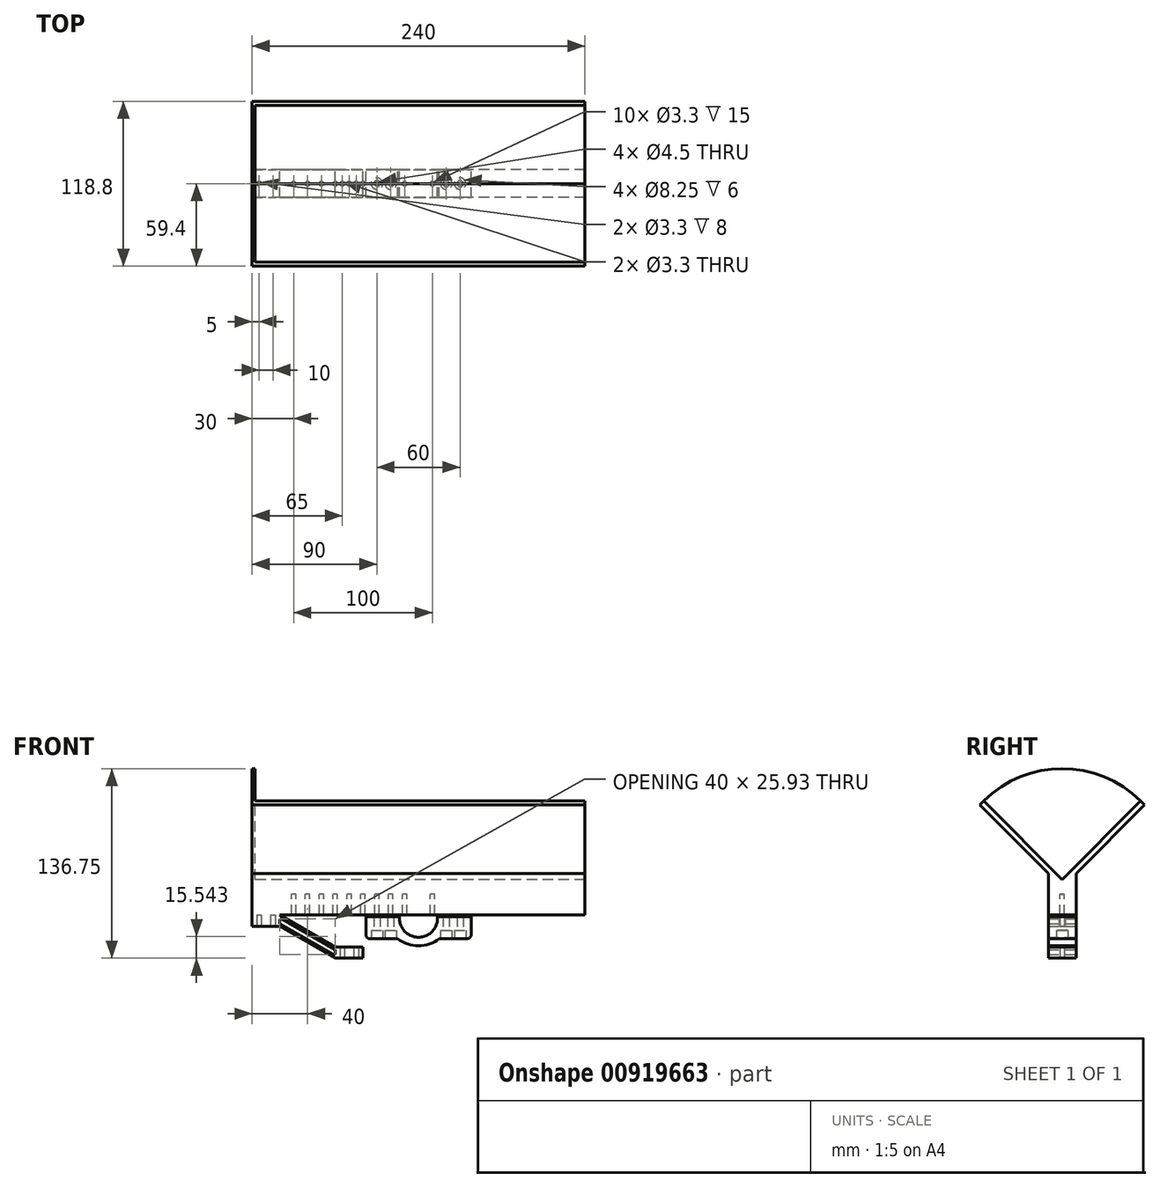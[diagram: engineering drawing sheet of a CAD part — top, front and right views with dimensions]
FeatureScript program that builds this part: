
annotation { "Feature Type Name" : "Feature", "Feature Type Description" : "" }
export const myFeature = defineFeature(function(context is Context, id is Id, definition is map)
    precondition{}
    {
        {
            var Q0;
            Q0=qCreatedBy(makeId("Right.planeOp"),FACE);
            var sketch = newSketch(context, id + "F0", { "sketchPlane" : qUnion([Q0])});
            skLineSegment(sketch, "E0.top", {"start": v(10, -15) * mm, "end": v(-10, -15) * mm});
            skLineSegment(sketch, "E0.left", {"start": v(10, 15) * mm, "end": v(10, -15) * mm});
            skLineSegment(sketch, "E0.right", {"start": v(-10, 15) * mm, "end": v(-10, -15) * mm});
            skPoint(sketch, "E0.middle", {"position": v(0, 0) * mm});
            skLineSegment(sketch, "E1", {"start": v(-10, 15) * mm, "end": v(-59.4, 64.4) * mm});
            skLineSegment(sketch, "E2", {"start": v(-59.4, 64.4) * mm, "end": v(-56.57, 67.23) * mm});
            skLineSegment(sketch, "E3", {"start": v(-56.57, 67.23) * mm, "end": v(0, 10.66) * mm});
            skLineSegment(sketch, "E4.MirrorCS", {"start": v(56.57, 67.23) * mm, "end": v(0, 10.66) * mm});
            skLineSegment(sketch, "E5.MirrorCS", {"start": v(10, 15) * mm, "end": v(59.4, 64.4) * mm});
            skLineSegment(sketch, "E6.MirrorCS", {"start": v(59.4, 64.4) * mm, "end": v(56.57, 67.23) * mm});
            skSolve(sketch);
        }
        {
            var Q0;
            Q0=qSketchRegion(id+"F0",true);
            extrude(context, id + "F1", {"entities" : qUnion([Q0]), "depth" : 120 * mm, "offsetDistance" : 25 * mm, "hasSecondDirection" : true, "secondDirectionOppositeDirection" : true, "secondDirectionDepth" : 120 * mm});
        }
        {
            var Q0;
            Q0=qCreatedBy(makeId("Front.planeOp"),FACE);
            var sketch = newSketch(context, id + "F2", { "sketchPlane" : qUnion([Q0])});
            skLineSegment(sketch, "E7.bottom", {"start": v(-120, -15) * mm, "end": v(-100, -15) * mm});
            skLineSegment(sketch, "E7.top", {"start": v(-120, -23) * mm, "end": v(-102.68, -23) * mm});
            skLineSegment(sketch, "E7.left", {"start": v(-120, -15) * mm, "end": v(-120, -23) * mm});
            skLineSegment(sketch, "E8.bottom", {"start": v(-60, -46.1) * mm, "end": v(-40, -46.1) * mm});
            skLineSegment(sketch, "E8.top", {"start": v(-57.32, -38.1) * mm, "end": v(-40, -38.1) * mm});
            skLineSegment(sketch, "E8.right", {"start": v(-40, -46.1) * mm, "end": v(-40, -38.1) * mm});
            skLineSegment(sketch, "E9", {"start": v(-97.68, -24.34) * mm, "end": v(-60, -46.1) * mm});
            skLineSegment(sketch, "E10", {"start": v(-100, -15) * mm, "end": v(-62.32, -36.75) * mm});
            skLineSegment(sketch, "E11", {"start": v(-100, -21.15) * mm, "end": v(-61.5, -43.38) * mm});
            skLineSegment(sketch, "E12", {"start": v(-60, -42.51) * mm, "end": v(-60, -39.94) * mm});
            skLineSegment(sketch, "E13", {"start": v(-60, -39.94) * mm, "end": v(-98.5, -17.71) * mm});
            skLineSegment(sketch, "E14", {"start": v(-100, -18.58) * mm, "end": v(-100, -21.15) * mm});
            skPoint(sketch, "E15", {"position": v(-115, -23) * mm});
            skPoint(sketch, "E16", {"position": v(-105, -23) * mm});
            skPoint(sketch, "E17", {"position": v(-55, -46.1) * mm});
            skPoint(sketch, "E18", {"position": v(-45, -46.1) * mm});
            skPoint(sketch, "E19.visualSharp", {"position": v(-100, -23) * mm});
            skArc(sketch, "E19.filletArc", {"start": v(-97.68, -24.34) * mm, "mid": v(-100.1, -23.34) * mm, "end": v(-102.68, -23) * mm});
            skPoint(sketch, "E20.visualSharp", {"position": v(-60, -38.1) * mm});
            skArc(sketch, "E20.filletArc", {"start": v(-62.32, -36.75) * mm, "mid": v(-59.9, -37.75) * mm, "end": v(-57.32, -38.1) * mm});
            skPoint(sketch, "E21.visualSharp", {"position": v(-100, -16.85) * mm});
            skArc(sketch, "E21.filletArc", {"start": v(-98.5, -17.71) * mm, "mid": v(-99.5, -17.71) * mm, "end": v(-100, -18.58) * mm});
            skPoint(sketch, "E22.visualSharp", {"position": v(-60, -44.25) * mm});
            skArc(sketch, "E22.filletArc", {"start": v(-61.5, -43.38) * mm, "mid": v(-60.5, -43.38) * mm, "end": v(-60, -42.51) * mm});
            skSolve(sketch);
        }
        {
            var Q0;
            Q0=qSketchRegion(id+"F2",true);
            extrude(context, id + "F3", {"entities" : qUnion([Q0]), "depth" : 10 * mm, "offsetDistance" : 25 * mm, "hasSecondDirection" : true, "secondDirectionOppositeDirection" : true, "secondDirectionDepth" : 10 * mm});
        }
        {
            var Q0;
            Q0=qCreatedBy(makeId("Top.planeOp"),FACE);
            var sketch = newSketch(context, id + "F4", { "sketchPlane" : qUnion([Q0])});
            skCircle(sketch, "E23", {"center": v(-90, 0) * mm, "radius": 2.5 * mm});
            skCircle(sketch, "E24.1.0.0", {"center": v(-80, 0) * mm, "radius": 2.5 * mm});
            skCircle(sketch, "E24.2.0.0", {"center": v(-70, 0) * mm, "radius": 2.5 * mm});
            skCircle(sketch, "E24.3.0.0", {"center": v(-60, 0) * mm, "radius": 2.5 * mm});
            skCircle(sketch, "E24.4.0.0", {"center": v(-50, 0) * mm, "radius": 2.5 * mm});
            skCircle(sketch, "E24.5.0.0", {"center": v(-40, 0) * mm, "radius": 2.5 * mm});
            skCircle(sketch, "E24.6.0.0", {"center": v(-30, 0) * mm, "radius": 2.5 * mm});
            skCircle(sketch, "E24.7.0.0", {"center": v(-20, 0) * mm, "radius": 2.5 * mm});
            skCircle(sketch, "E24.8.0.0", {"center": v(-10, 0) * mm, "radius": 2.5 * mm});
            skCircle(sketch, "E24.9.0.0", {"center": v(0, 0) * mm, "radius": 2.5 * mm});
            skCircle(sketch, "E24.10.0.0", {"center": v(10, 0) * mm, "radius": 2.5 * mm});
            skCircle(sketch, "E24.11.0.0", {"center": v(20, 0) * mm, "radius": 2.5 * mm});
            skCircle(sketch, "E24.12.0.0", {"center": v(30, 0) * mm, "radius": 2.5 * mm});
            skCircle(sketch, "E24.13.0.0", {"center": v(40, 0) * mm, "radius": 2.5 * mm});
            skCircle(sketch, "E24.14.0.0", {"center": v(50, 0) * mm, "radius": 2.5 * mm});
            skCircle(sketch, "E24.15.0.0", {"center": v(60, 0) * mm, "radius": 2.5 * mm});
            skCircle(sketch, "E24.16.0.0", {"center": v(70, 0) * mm, "radius": 2.5 * mm});
            skLineSegment(sketch, "E24.direction1", {"start": v(-90, 0) * mm, "end": v(-80, 0) * mm, "construction": true});
            skCircle(sketch, "E25.0.17.0", {"center": v(80, 0) * mm, "radius": 2.5 * mm});
            skCircle(sketch, "E25.0.18.0", {"center": v(90, 0) * mm, "radius": 2.5 * mm});
            skSolve(sketch);
        }
        {
            var Q0;
            Q0=sQuery(id+"F4.wireOp",VERTEX,"E23.center");
            var Q1;
            Q1=sQuery(id+"F4.wireOp",VERTEX,"E24.1.0.0.center");
            var Q2;
            Q2=sQuery(id+"F4.wireOp",VERTEX,"E24.2.0.0.center");
            var Q3;
            Q3=sQuery(id+"F4.wireOp",VERTEX,"E24.3.0.0.center");
            var Q4;
            Q4=sQuery(id+"F4.wireOp",VERTEX,"E24.4.0.0.center");
            var Q5;
            Q5=sQuery(id+"F4.wireOp",VERTEX,"E24.5.0.0.center");
            var Q6;
            Q6=sQuery(id+"F4.wireOp",VERTEX,"E24.6.0.0.center");
            var Q7;
            Q7=sQuery(id+"F4.wireOp",VERTEX,"E24.7.0.0.center");
            var Q8;
            Q8=sQuery(id+"F4.wireOp",VERTEX,"E24.8.0.0.center");
            var Q9;
            Q9=sQuery(id+"F4.wireOp",VERTEX,"E24.10.0.0.center");
            var Q10;
            Q10=makeQuery(id+"F1.opExtrude","SWEPT_BODY",BODY,{"disambiguationData":[OSD([sQuery(id+"F0.wireOp",EDGE,"E0.top"),sQuery(id+"F0.wireOp",EDGE,"E0.left"),sQuery(id+"F0.wireOp",EDGE,"E0.right"),sQuery(id+"F0.wireOp",EDGE,"E1"),sQuery(id+"F0.wireOp",EDGE,"E2"),sQuery(id+"F0.wireOp",EDGE,"E3"),sQuery(id+"F0.wireOp",EDGE,"E4.MirrorCS"),sQuery(id+"F0.wireOp",EDGE,"E5.MirrorCS"),sQuery(id+"F0.wireOp",EDGE,"E6.MirrorCS")])]});
            hole(context, id + "F5", {"style" : HoleStyle.SIMPLE, "endStyle" : HoleEndStyle.THROUGH, "standardTappedOrClearance" : lookupTablePath({ "standard" : "ISO", "fit" : "Normal", "size" : "M3", "type" : "Clearance" }), "standardBlindInLast" : lookupTablePath({ "fit" : "Standard", "standard" : "ISO", "size" : "M3", "type" : "Clearance" }), "holeDiameter" : 3.3 * mm, "majorDiameter" : 5 * mm, "isTappedThrough" : true, "tappedDepth" : 12 * mm, "tapClearance" : 3, "locations" : qUnion([Q0, Q1, Q2, Q3, Q4, Q5, Q6, Q7, Q8, Q9]), "scope" : qUnion([Q10])});
        }
        {
            var Q0;
            Q0=makeQuery(id+"F3.opExtrude","SWEPT_FACE",FACE,{"disambiguationData":[OSD([sQuery(id+"F2.wireOp",EDGE,"E7.top")])]});
            var sketch = newSketch(context, id + "F6", { "sketchPlane" : qUnion([Q0])});
            skCircle(sketch, "E26", {"center": v(-110, 0) * mm, "radius": 10 * mm});
            skLineSegment(sketch, "E27", {"start": v(-120, 0) * mm, "end": v(-110, 0) * mm, "construction": true});
            skLineSegment(sketch, "E28", {"start": v(-100, 0) * mm, "end": v(-110, 0) * mm, "construction": true});
            skPoint(sketch, "E29", {"position": v(-115, 0) * mm});
            skPoint(sketch, "E30", {"position": v(-105, 0) * mm});
            skSolve(sketch);
        }
        {
            var Q0;
            Q0=makeQuery(id+"F3.opExtrude","SWEPT_FACE",FACE,{"disambiguationData":[OSD([sQuery(id+"F2.wireOp",EDGE,"E8.bottom")])]});
            var sketch = newSketch(context, id + "F7", { "sketchPlane" : qUnion([Q0])});
            skCircle(sketch, "E31", {"center": v(-50, 0) * mm, "radius": 10 * mm});
            skLineSegment(sketch, "E32", {"start": v(-60, 0) * mm, "end": v(-50, 0) * mm, "construction": true});
            skLineSegment(sketch, "E33", {"start": v(-40, 0) * mm, "end": v(-50, 0) * mm, "construction": true});
            skPoint(sketch, "E34", {"position": v(-55, 0) * mm});
            skPoint(sketch, "E35", {"position": v(-45, 0) * mm});
            skSolve(sketch);
        }
        {
            var Q0;
            Q0=sQuery(id+"F7.wireOp",VERTEX,"E35");
            var Q1;
            Q1=sQuery(id+"F7.wireOp",VERTEX,"E34");
            var Q2;
            Q2=sQuery(id+"F6.wireOp",VERTEX,"E30");
            var Q3;
            Q3=sQuery(id+"F6.wireOp",VERTEX,"E29");
            var Q4;
            Q4=makeQuery(id+"F3.opExtrude","SWEPT_BODY",BODY,{"disambiguationData":[OSD([sQuery(id+"F2.wireOp",EDGE,"E7.bottom"),sQuery(id+"F2.wireOp",EDGE,"E7.top"),sQuery(id+"F2.wireOp",EDGE,"E7.left"),sQuery(id+"F2.wireOp",EDGE,"E8.bottom"),sQuery(id+"F2.wireOp",EDGE,"E8.top"),sQuery(id+"F2.wireOp",EDGE,"E8.right"),sQuery(id+"F2.wireOp",EDGE,"E9"),sQuery(id+"F2.wireOp",EDGE,"E10"),sQuery(id+"F2.wireOp",EDGE,"E11"),sQuery(id+"F2.wireOp",EDGE,"E12"),sQuery(id+"F2.wireOp",EDGE,"E13"),sQuery(id+"F2.wireOp",EDGE,"E14")])]});
            hole(context, id + "F8", {"style" : HoleStyle.SIMPLE, "endStyle" : HoleEndStyle.THROUGH, "standardTappedOrClearance" : lookupTablePath({ "standard" : "ISO", "fit" : "Normal", "size" : "M3", "type" : "Clearance" }), "standardBlindInLast" : lookupTablePath({ "fit" : "Standard", "standard" : "ISO", "size" : "M3", "type" : "Clearance" }), "holeDiameter" : 3.3 * mm, "majorDiameter" : 5 * mm, "isTappedThrough" : true, "tappedDepth" : 12 * mm, "tapClearance" : 3, "locations" : qUnion([Q0, Q1, Q2, Q3]), "scope" : qUnion([Q4])});
        }
        {
            var Q0;
            Q0=makeQuery(id+"F1.opExtrude","CAP_FACE",FACE,{"disambiguationData":[OSD([sQuery(id+"F0.wireOp",EDGE,"E0.top"),sQuery(id+"F0.wireOp",EDGE,"E0.left"),sQuery(id+"F0.wireOp",EDGE,"E0.right"),sQuery(id+"F0.wireOp",EDGE,"E1"),sQuery(id+"F0.wireOp",EDGE,"E2"),sQuery(id+"F0.wireOp",EDGE,"E3"),sQuery(id+"F0.wireOp",EDGE,"E4.MirrorCS"),sQuery(id+"F0.wireOp",EDGE,"E5.MirrorCS"),sQuery(id+"F0.wireOp",EDGE,"E6.MirrorCS")])],"isStart":true});
            var sketch = newSketch(context, id + "F9", { "sketchPlane" : qUnion([Q0])});
            skLineSegment(sketch, "E36", {"start": v(-59.4, 64.4) * mm, "end": v(-10, 15) * mm});
            skLineSegment(sketch, "E37", {"start": v(-10, 15) * mm, "end": v(-10, -15) * mm});
            skLineSegment(sketch, "E38", {"start": v(-10, -15) * mm, "end": v(10, -15) * mm});
            skLineSegment(sketch, "E39", {"start": v(10, -15) * mm, "end": v(10, 15) * mm});
            skLineSegment(sketch, "E40", {"start": v(10, 15) * mm, "end": v(59.4, 64.4) * mm});
            skLineSegment(sketch, "E41", {"start": v(-59.4, 64.4) * mm, "end": v(-56.57, 67.23) * mm});
            skLineSegment(sketch, "E42", {"start": v(59.4, 64.4) * mm, "end": v(56.57, 67.23) * mm});
            skArc(sketch, "E43", {"start": v(-56.57, 67.23) * mm, "mid": v(0, 90.66) * mm, "end": v(56.57, 67.23) * mm});
            skSolve(sketch);
        }
        {
            var Q0;
            Q0=qSketchRegion(id+"F9",true);
            extrude(context, id + "F10", {"entities" : qUnion([Q0]), "operationType" : NewBodyOperationType.ADD, "oppositeDirection" : true, "depth" : 2 * mm, "offsetDistance" : 25 * mm});
        }
        {
            var Q0;
            Q0=qCreatedBy(makeId("Front.planeOp"),FACE);
            var sketch = newSketch(context, id + "F11", { "sketchPlane" : qUnion([Q0])});
            skArc(sketch, "E44", {"start": v(-13.67, -16) * mm, "mid": v(0, -31) * mm, "end": v(13.67, -16) * mm});
            skLineSegment(sketch, "E45", {"start": v(-13.67, -16) * mm, "end": v(-38, -16) * mm});
            skLineSegment(sketch, "E46", {"start": v(-38, -16) * mm, "end": v(-38, -32) * mm});
            skLineSegment(sketch, "E47", {"start": v(-38, -32) * mm, "end": v(-15, -32) * mm});
            skLineSegment(sketch, "E48.MirrorCS", {"start": v(13.67, -16) * mm, "end": v(38, -16) * mm});
            skLineSegment(sketch, "E49.MirrorCS", {"start": v(38, -32) * mm, "end": v(15, -32) * mm});
            skLineSegment(sketch, "E50.MirrorCS", {"start": v(38, -16) * mm, "end": v(38, -32) * mm});
            skArc(sketch, "E51", {"start": v(-15, -32) * mm, "mid": v(0, -37) * mm, "end": v(15, -32) * mm});
            skSolve(sketch);
        }
        {
            var Q0;
            Q0=qSketchRegion(id+"F11",true);
            extrude(context, id + "F12", {"entities" : qUnion([Q0]), "endBound" : BoundingType.SYMMETRIC, "depth" : 20 * mm, "offsetDistance" : 25 * mm});
        }
        {
            var Q0;
            Q0=makeQuery(id+"F12.opExtrude","SWEPT_FACE",FACE,{"disambiguationData":[OSD([sQuery(id+"F11.wireOp",EDGE,"E47")])]});
            var sketch = newSketch(context, id + "F13", { "sketchPlane" : qUnion([Q0])});
            skLineSegment(sketch, "E52", {"start": v(-30, 0) * mm, "end": v(-20, 0) * mm, "construction": true});
            skLineSegment(sketch, "E53.MirrorCS", {"start": v(30, 0) * mm, "end": v(20, 0) * mm, "construction": true});
            skSolve(sketch);
        }
        {
            var Q0;
            Q0=sQuery(id+"F13.wireOp",VERTEX,"E52.start");
            var Q1;
            Q1=sQuery(id+"F13.wireOp",VERTEX,"E52.end");
            var Q2;
            Q2=sQuery(id+"F13.wireOp",VERTEX,"E53.MirrorCS.end");
            var Q3;
            Q3=sQuery(id+"F13.wireOp",VERTEX,"E53.MirrorCS.start");
            var Q4;
            Q4=makeQuery(id+"F12.opExtrude","SWEPT_BODY",BODY,{"disambiguationData":[OSD([sQuery(id+"F11.wireOp",EDGE,"E44"),sQuery(id+"F11.wireOp",EDGE,"E45"),sQuery(id+"F11.wireOp",EDGE,"E46"),sQuery(id+"F11.wireOp",EDGE,"E47"),sQuery(id+"F11.wireOp",EDGE,"E48.MirrorCS"),sQuery(id+"F11.wireOp",EDGE,"E49.MirrorCS"),sQuery(id+"F11.wireOp",EDGE,"E50.MirrorCS"),sQuery(id+"F11.wireOp",EDGE,"E51")])]});
            hole(context, id + "F14", {"style" : HoleStyle.C_BORE, "endStyle" : HoleEndStyle.BLIND, "holeDiameter" : 4.5 * mm, "cBoreDiameter" : 8.25 * mm, "cBoreDepth" : 6 * mm, "majorDiameter" : 5 * mm, "holeDepth" : 40 * mm, "isTappedThrough" : true, "tappedDepth" : 12 * mm, "tapClearance" : 3, "locations" : qUnion([Q0, Q1, Q2, Q3]), "scope" : qUnion([Q4])});
        }
        {
            var Q0;
            Q0=makeQuery(id+"F12.opExtrude","SWEPT_EDGE",EDGE,{"disambiguationData":[OSD([sQuery(id+"F11.wireOp",EDGE,"E46"),sQuery(id+"F11.wireOp",EDGE,"E47")])]});
            var Q1;
            Q1=makeQuery(id+"F12.opExtrude","SWEPT_EDGE",EDGE,{"disambiguationData":[OSD([sQuery(id+"F11.wireOp",EDGE,"E49.MirrorCS"),sQuery(id+"F11.wireOp",EDGE,"E50.MirrorCS")])]});
            fillet(context, id + "F15", {"entities" : qUnion([Q0, Q1]), "radius" : 3 * mm, "tangentPropagation" : true, "allowEdgeOverflow" : false});
        }
    });
